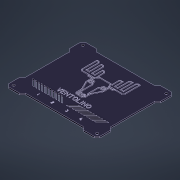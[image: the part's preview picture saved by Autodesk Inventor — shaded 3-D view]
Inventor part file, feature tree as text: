
AUTODESK INVENTOR PART (.ipt)
format: ipt  version: 2021.3 (Build 253353000, 353)  size: 1,401,344 bytes
history: native  units: mm
features: sketch x5, projected_geometry x4, extrude x2, mirror x2, chamfer x1, emboss x1, other x1, hole x1
ambient origin geometry x8: Origin, YZ Plane, XZ Plane, XY Plane, X Axis, Y Axis, Z Axis, Center Point
bodies: Solid1 (feature_tree)
feature tree (17):
  extrude  "Extrusion1"  Depth=100.0mm
  extrude  "Extrusion2"  Depth=2.0mm
  mirror  "Mirror1"
  chamfer  "Chamfer1"  Distance=2.0mm
  emboss  "Emboss1"
  other  "Grill1"
  mirror  "Mirror2"
  hole  "Hole1"  [1 undecoded]
  sketch  "Sketch1"  dims[d0=120.0mm d1=100.0mm]
  sketch  "Sketch2"  dims[d2=4.0mm d3=15.0mm d4=2.0mm d5=0.0mm]
  projected_geometry  "Projected Loop1"
  sketch  "Sketch3"  dims[d74=10.0mm d75=4.0mm]
  projected_geometry  "Projected Loop2"
  sketch  "Sketch4"  dims[d76=2.0mm]
  projected_geometry  "Projected Loop3"
  sketch  "Sketch5"  dims[d77=4.0mm d78=4.0mm d79=4.0mm d80=135.0deg d81=19.0mm d82=4.0mm d83=4.0mm d85=2.0mm d86=8.0mm d87=2.0mm d89=2.0mm d90=6.0mm d91=5.0mm d92=3.0mm d93=8.0mm d94=12.0mm d95=6.0mm d96=6.0mm d98=2.0mm d99=4.0mm d100=2.0mm d101=8.0mm d104=1.0mm d105=1.0mm d106=2.0mm d107=1.0mm d108=1.0mm d109=2.0mm d110=1.0mm d111=0.25mm d112=0.25mm d113=0.25mm d114=0.25mm d115=0.25mm d116=0.25mm d117=0.256mm d118=0.25mm d119=0.25mm d120=0.25mm d121=0.25mm d122=0.25mm d123=0.25mm d124=0.25mm d125=0.5mm d126=0.0mm d127=0.5mm d128=2.0mm d129=45.0deg d130=15.0mm d131=15.0mm d132=15.0mm d133=5.0mm d135=5.0mm d141=22.0mm d142=12.0mm d143=50.0mm d144=0.5mm d145=0.0mm d146=9.0mm d147=42.0mm d148=2.5mm d149=14.0mm d150=135.0deg d151=5.0mm d152=5.0mm d153=3.0mm d154=100.0mm d156=4.0mm d157=10.0mm d159=10.0mm d161=1.414214mm d162=2.0mm d163=0.0mm d164=1.0mm d165=2.0mm d166=0.0mm d167=1.414214mm d168=0.0mm d169=0.0mm d170=1.0mm d171=0.0mm d172=0.0mm d173=0.0mm d174=19.8mm d175=1.37mm d176=1.37mm d177=1.37mm d178=1.37mm d179=3.4mm d180=6.0mm d181=4.0mm d182=2.0mm d183=90.0deg d184=5.0mm d185=0.0mm]
  projected_geometry  "Projected Loop4"
note: 1 required parameter value undecoded (feature->parameter linkage not recoverable at this tier; creation-order binding heuristic only, values carry confidence <= 0.55)
